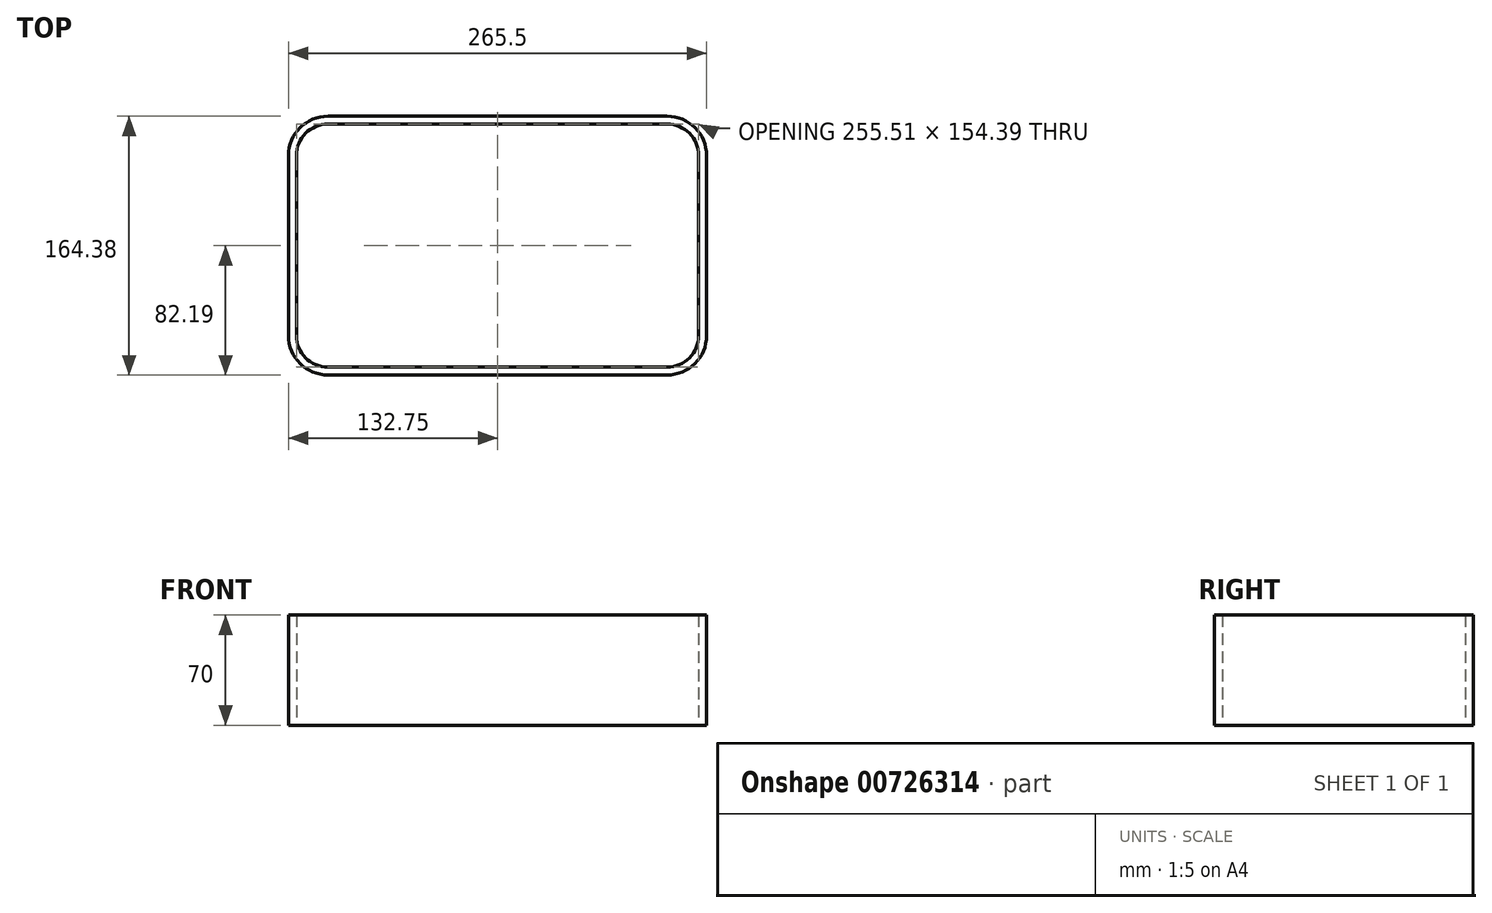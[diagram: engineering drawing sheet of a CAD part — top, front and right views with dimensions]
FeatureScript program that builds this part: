
annotation { "Feature Type Name" : "Feature", "Feature Type Description" : "" }
export const myFeature = defineFeature(function(context is Context, id is Id, definition is map)
    precondition{}
    {
        {
            var Q0;
            Q0=qCreatedBy(makeId("Top.planeOp"),FACE);
            var sketch = newSketch(context, id + "F0", { "sketchPlane" : qUnion([Q0])});
            skLineSegment(sketch, "E0.bottom", {"start": v(107.75, -77.2) * mm, "end": v(-107.75, -77.2) * mm});
            skLineSegment(sketch, "E0.top", {"start": v(107.75, 77.2) * mm, "end": v(-107.75, 77.2) * mm});
            skLineSegment(sketch, "E0.left", {"start": v(127.75, -57.2) * mm, "end": v(127.75, 57.2) * mm});
            skLineSegment(sketch, "E0.right", {"start": v(-127.75, -57.2) * mm, "end": v(-127.75, 57.2) * mm});
            skPoint(sketch, "E0.middle", {"position": v(0, 0) * mm});
            skPoint(sketch, "E1.visualSharp", {"position": v(-127.75, 77.2) * mm});
            skArc(sketch, "E1.filletArc", {"start": v(-107.75, 77.2) * mm, "mid": v(-121.9, 71.34) * mm, "end": v(-127.75, 57.2) * mm});
            skPoint(sketch, "E2.visualSharp", {"position": v(-127.75, -77.2) * mm});
            skArc(sketch, "E2.filletArc", {"start": v(-127.75, -57.2) * mm, "mid": v(-121.9, -71.34) * mm, "end": v(-107.75, -77.2) * mm});
            skPoint(sketch, "E3.visualSharp", {"position": v(127.75, 77.2) * mm});
            skArc(sketch, "E3.filletArc", {"start": v(127.75, 57.2) * mm, "mid": v(121.9, 71.34) * mm, "end": v(107.75, 77.2) * mm});
            skPoint(sketch, "E4.visualSharp", {"position": v(127.75, -77.2) * mm});
            skArc(sketch, "E4.filletArc", {"start": v(107.75, -77.2) * mm, "mid": v(121.9, -71.34) * mm, "end": v(127.75, -57.2) * mm});
            skArc(sketch, "E5.0", {"start": v(132.75, 57.2) * mm, "mid": v(125.43, 74.87) * mm, "end": v(107.75, 82.2) * mm});
            skLineSegment(sketch, "E5.1", {"start": v(132.75, -57.2) * mm, "end": v(132.75, 57.2) * mm});
            skLineSegment(sketch, "E5.2", {"start": v(107.75, 82.2) * mm, "end": v(-107.75, 82.2) * mm});
            skArc(sketch, "E5.3", {"start": v(107.75, -82.2) * mm, "mid": v(125.43, -74.87) * mm, "end": v(132.75, -57.2) * mm});
            skArc(sketch, "E5.4", {"start": v(-107.75, 82.2) * mm, "mid": v(-125.43, 74.87) * mm, "end": v(-132.75, 57.2) * mm});
            skLineSegment(sketch, "E5.5", {"start": v(-132.75, -57.2) * mm, "end": v(-132.75, 57.2) * mm});
            skArc(sketch, "E5.6", {"start": v(-132.75, -57.2) * mm, "mid": v(-125.43, -74.87) * mm, "end": v(-107.75, -82.2) * mm});
            skLineSegment(sketch, "E5.7", {"start": v(107.75, -82.2) * mm, "end": v(-107.75, -82.2) * mm});
            skSolve(sketch);
        }
        {
            var Q0;
            Q0=makeQuery(id+"F0.imprint","IMPRINT",FACE,{"disambiguationData":[TD([[makeQuery(id+"F0.imprint","IMPRINT",EDGE,{"derivedFrom":sQuery(id+"F0.wireOp",EDGE,"E0.bottom")}),1.0]])]});
            extrude(context, id + "F1", {"entities" : qUnion([Q0]), "depth" : 70 * mm, "offsetDistance" : 25 * mm});
        }
    });
